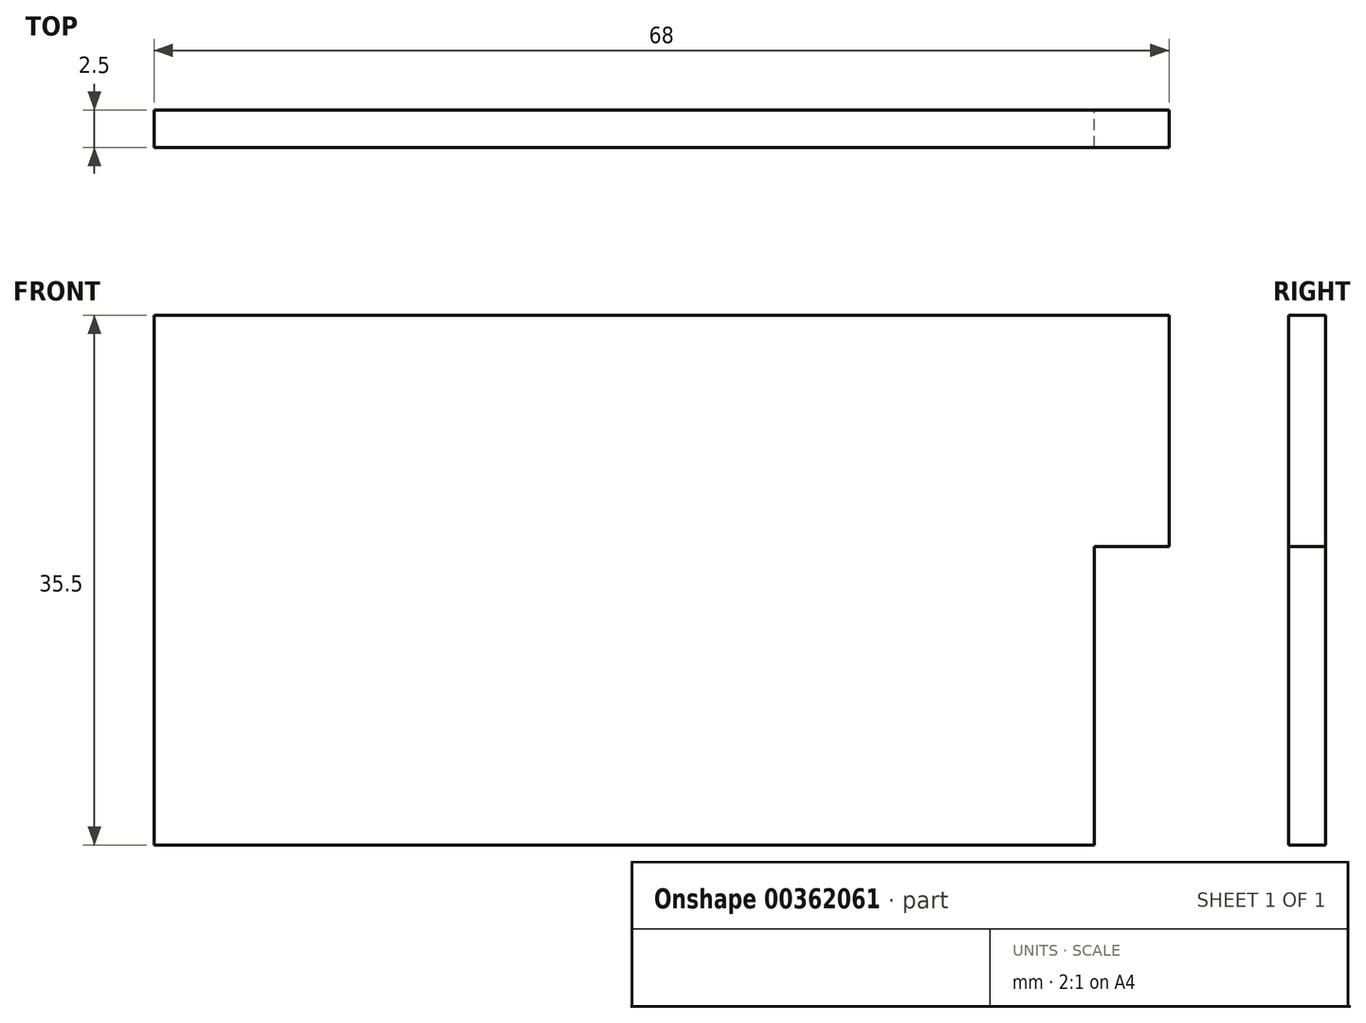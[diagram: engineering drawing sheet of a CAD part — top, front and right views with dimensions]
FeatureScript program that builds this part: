
annotation { "Feature Type Name" : "Feature", "Feature Type Description" : "" }
export const myFeature = defineFeature(function(context is Context, id is Id, definition is map)
    precondition{}
    {
        {
            var Q0;
            Q0=qCreatedBy(makeId("Front.planeOp"),FACE);
            var sketch = newSketch(context, id + "F0", { "sketchPlane" : qUnion([Q0])});
            skLineSegment(sketch, "E0", {"start": v(0, 0) * mm, "end": v(0, 35.5) * mm});
            skLineSegment(sketch, "E1", {"start": v(0, 35.5) * mm, "end": v(68, 35.5) * mm});
            skLineSegment(sketch, "E2", {"start": v(68, 35.5) * mm, "end": v(68, 20) * mm});
            skLineSegment(sketch, "E3", {"start": v(68, 20) * mm, "end": v(63, 20) * mm});
            skLineSegment(sketch, "E4", {"start": v(63, 20) * mm, "end": v(63, 0) * mm});
            skLineSegment(sketch, "E5", {"start": v(63, 0) * mm, "end": v(0, 0) * mm});
            skSolve(sketch);
        }
        {
            var Q0;
            Q0 = qSketchRegion(id + "F0", true);
            extrude(context, id + "F1", {"entities" : qUnion([Q0]), "depth" : 2.5 * mm});
        }
    });
